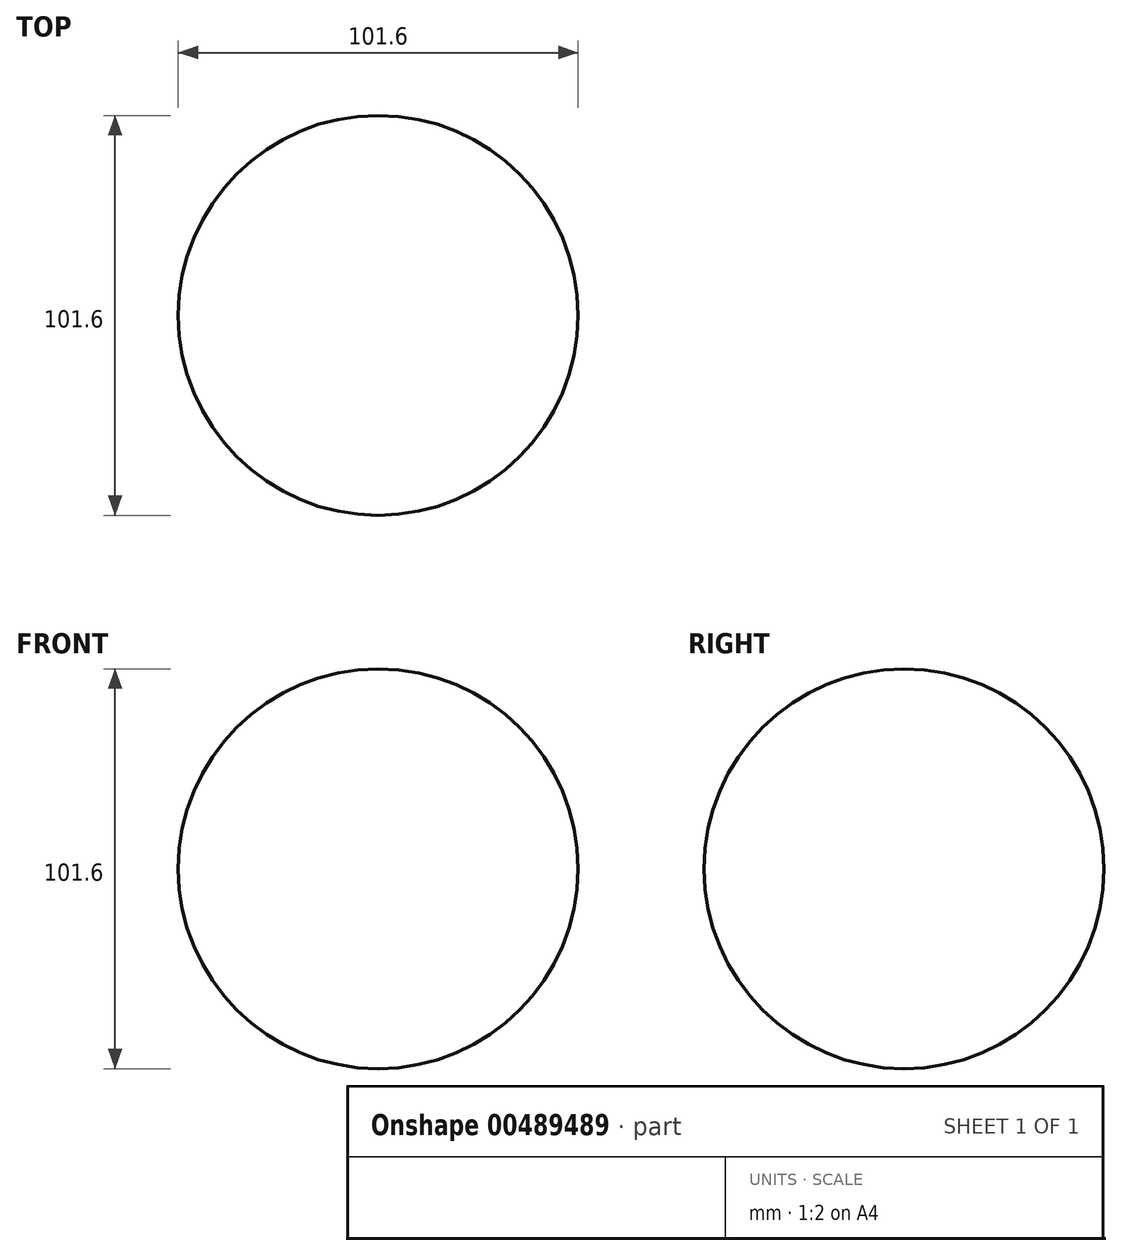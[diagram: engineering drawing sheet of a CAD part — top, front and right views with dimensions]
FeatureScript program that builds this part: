
annotation { "Feature Type Name" : "Feature", "Feature Type Description" : "" }
export const myFeature = defineFeature(function(context is Context, id is Id, definition is map)
    precondition{}
    {
        {
            var Q0;
            Q0=qCreatedBy(makeId("Front.planeOp"),FACE);
            var sketch = newSketch(context, id + "F0", { "sketchPlane" : qUnion([Q0])});
            skCircle(sketch, "E0", {"center": v(0, 0) * mm, "radius": 50.8 * mm});
            skSolve(sketch);
        }
        {
            var Q0;
            Q0=makeQuery(id+"F0.imprint","IMPRINT",FACE,{"disambiguationData":[TD([[makeQuery(id+"F0.imprint","IMPRINT",EDGE,{"derivedFrom":sQuery(id+"F0.wireOp",EDGE,"E0")}),1.0]])]});
            extrude(context, id + "F1", {"entities" : qUnion([Q0]), "depth" : 50.8 * mm});
        }
        {
            var Q0;
            Q0=makeQuery(id+"F1.opExtrude","CAP_EDGE",EDGE,{"disambiguationData":[OSD([sQuery(id+"F0.wireOp",EDGE,"E0")])],"isStart":false});
            fillet(context, id + "F2", {"entities" : qUnion([Q0]), "radius" : 50.8 * mm, "tangentPropagation" : true, "allowEdgeOverflow" : false});
        }
        {
            var Q0;
            Q0=qCreatedBy(makeId("Front.planeOp"),FACE);
            var sketch = newSketch(context, id + "F3", { "sketchPlane" : qUnion([Q0])});
            skLineSegment(sketch, "E1", {"start": v(0, 76.96) * mm, "end": v(0, -76.1) * mm});
            skArc(sketch, "E2", {"start": v(0, -50.8) * mm, "mid": v(50.8, 0) * mm, "end": v(0, 50.8) * mm});
            skSolve(sketch);
        }
        {
            var Q0;
            Q0 = qSketchRegion(id + "F3", true);
            var Q1;
            Q1=sQuery(id+"F3.wireOp",EDGE,"E1");
            revolve(context, id + "F4", {"operationType" : NewBodyOperationType.ADD, "entities" : qUnion([Q0]), "axis" : qUnion([Q1]), "revolveType" : RevolveType.FULL});
        }
    });
